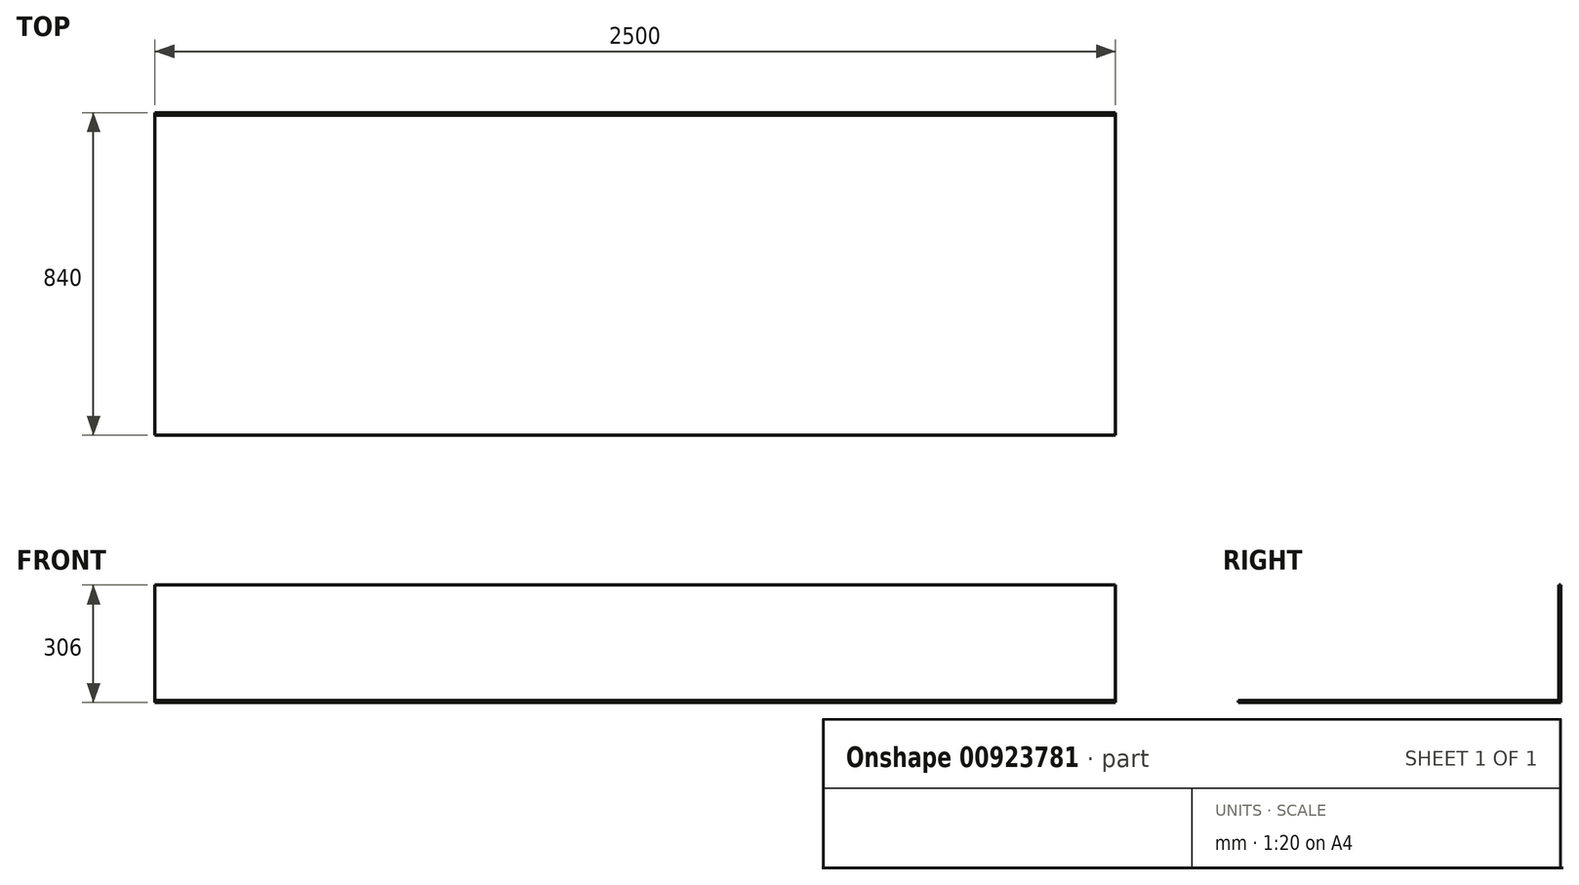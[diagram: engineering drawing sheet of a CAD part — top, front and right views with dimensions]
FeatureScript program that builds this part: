
annotation { "Feature Type Name" : "Feature", "Feature Type Description" : "" }
export const myFeature = defineFeature(function(context is Context, id is Id, definition is map)
    precondition{}
    {
        {
            var Q0;
            Q0=qCreatedBy(makeId("Top.planeOp"),FACE);
            var sketch = newSketch(context, id + "F0", { "sketchPlane" : qUnion([Q0])});
            skLineSegment(sketch, "E0.bottom", {"start": v(-98.8, -18.48) * mm, "end": v(2401.2, -18.48) * mm});
            skLineSegment(sketch, "E0.top", {"start": v(-98.8, 821.52) * mm, "end": v(2401.2, 821.52) * mm});
            skLineSegment(sketch, "E0.left", {"start": v(-98.8, -18.48) * mm, "end": v(-98.8, 821.52) * mm});
            skLineSegment(sketch, "E0.right", {"start": v(2401.2, -18.48) * mm, "end": v(2401.2, 821.52) * mm});
            skSolve(sketch);
        }
        {
            var Q0;
            Q0=makeQuery(id+"F0.imprint","IMPRINT",FACE,{"disambiguationData":[TD([[makeQuery(id+"F0.imprint","IMPRINT",EDGE,{"derivedFrom":sQuery(id+"F0.wireOp",EDGE,"E0.bottom")}),1.0]])]});
            extrude(context, id + "F1", {"entities" : qUnion([Q0]), "depth" : 6 * mm, "offsetDistance" : 25 * mm});
        }
        {
            var Q0;
            Q0=makeQuery(id+"F1.opExtrude","CAP_FACE",FACE,{"disambiguationData":[OSD([sQuery(id+"F0.wireOp",EDGE,"E0.bottom"),sQuery(id+"F0.wireOp",EDGE,"E0.top"),sQuery(id+"F0.wireOp",EDGE,"E0.left"),sQuery(id+"F0.wireOp",EDGE,"E0.right")])],"isStart":false});
            var sketch = newSketch(context, id + "F2", { "sketchPlane" : qUnion([Q0])});
            skLineSegment(sketch, "E1.bottom", {"start": v(-98.8, 821.52) * mm, "end": v(2401.2, 821.52) * mm});
            skLineSegment(sketch, "E1.top", {"start": v(-98.8, 815.52) * mm, "end": v(2401.2, 815.52) * mm});
            skLineSegment(sketch, "E1.left", {"start": v(-98.8, 821.52) * mm, "end": v(-98.8, 815.52) * mm});
            skLineSegment(sketch, "E1.right", {"start": v(2401.2, 821.52) * mm, "end": v(2401.2, 815.52) * mm});
            skSolve(sketch);
        }
        {
            var Q0;
            Q0 = qSketchRegion(id + "F2", true);
            extrude(context, id + "F3", {"entities" : qUnion([Q0]), "operationType" : NewBodyOperationType.ADD, "depth" : 25 * mm, "offsetDistance" : 25 * mm});
        }
        {
            var Q0;
            Q0=makeQuery(id+"F3.opExtrude","CAP_FACE",FACE,{"disambiguationData":[OSD([sQuery(id+"F2.wireOp",EDGE,"E1.bottom"),sQuery(id+"F2.wireOp",EDGE,"E1.top"),sQuery(id+"F2.wireOp",EDGE,"E1.left"),sQuery(id+"F2.wireOp",EDGE,"E1.right")])],"isStart":false});
            extrude(context, id + "F4", {"entities" : qUnion([Q0]), "operationType" : NewBodyOperationType.ADD, "depth" : 275 * mm, "offsetDistance" : 25 * mm});
        }
    });
